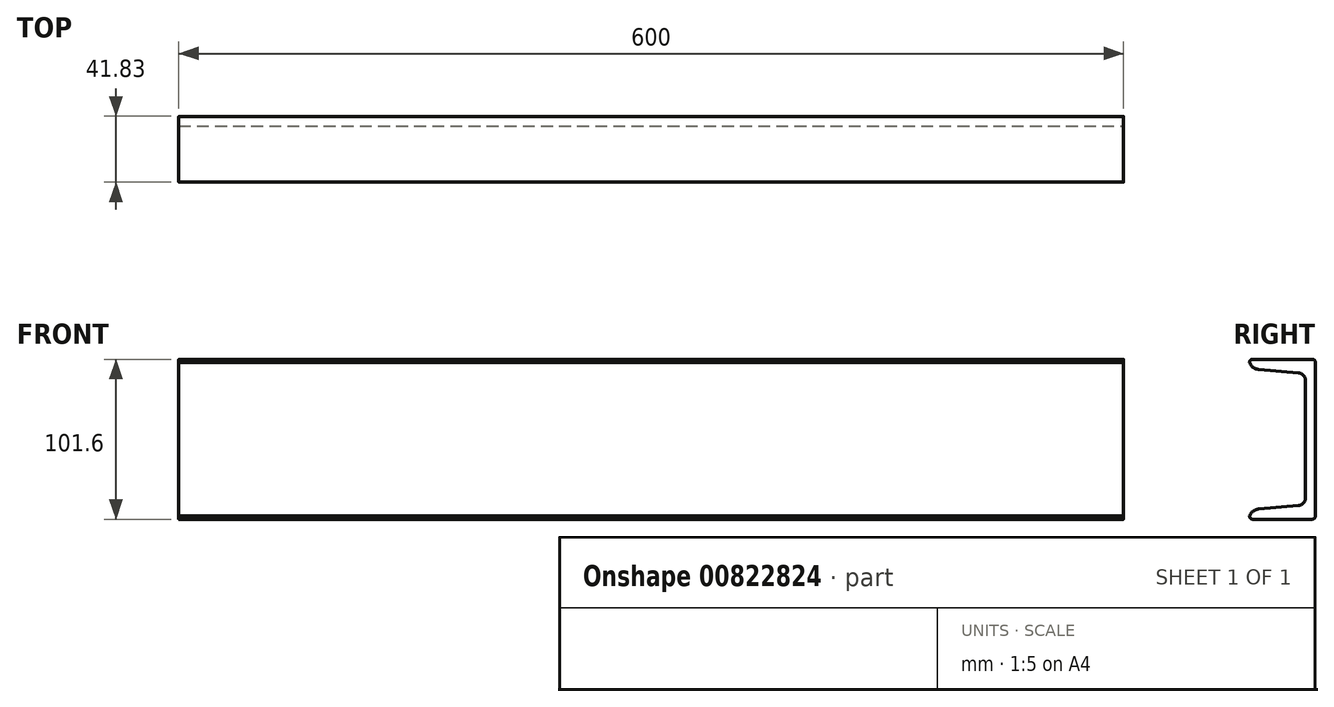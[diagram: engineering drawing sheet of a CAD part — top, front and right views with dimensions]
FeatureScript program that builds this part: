
annotation { "Feature Type Name" : "Feature", "Feature Type Description" : "" }
export const myFeature = defineFeature(function(context is Context, id is Id, definition is map)
    precondition{}
    {
        {
            var Q0;
            Q0=qCreatedBy(makeId("Right.planeOp"),FACE);
            var sketch = newSketch(context, id + "F0", { "sketchPlane" : qUnion([Q0])});
            skLineSegment(sketch, "E0.bottom", {"start": v(-18.91, -50.8) * mm, "end": v(18.92, -50.8) * mm});
            skLineSegment(sketch, "E0.top", {"start": v(-18.91, 50.8) * mm, "end": v(18.92, 50.8) * mm});
            skLineSegment(sketch, "E0.left", {"start": v(-20.91, -44.84) * mm, "end": v(-20.91, 44.84) * mm, "construction": true});
            skLineSegment(sketch, "E0.right", {"start": v(20.92, -48.8) * mm, "end": v(20.92, 48.8) * mm});
            skPoint(sketch, "E0.middle", {"position": v(0, 0) * mm});
            skLineSegment(sketch, "E1", {"start": v(-20.91, -44.84) * mm, "end": v(10.08, -42.12) * mm});
            skLineSegment(sketch, "E2", {"start": v(14.64, -37.14) * mm, "end": v(14.64, 37.14) * mm});
            skLineSegment(sketch, "E3", {"start": v(10.08, 42.12) * mm, "end": v(-20.92, 44.84) * mm});
            skLineSegment(sketch, "E4", {"start": v(-20.91, 44.84) * mm, "end": v(-20.91, 48.8) * mm});
            skLineSegment(sketch, "E5", {"start": v(-20.91, -44.84) * mm, "end": v(-20.91, -48.8) * mm});
            skPoint(sketch, "E6", {"position": v(-3.13, -43.28) * mm});
            skPoint(sketch, "E7", {"position": v(-3.14, 43.28) * mm});
            skPoint(sketch, "E8.visualSharp", {"position": v(20.92, 50.8) * mm});
            skArc(sketch, "E8.filletArc", {"start": v(20.92, 48.8) * mm, "mid": v(20.33, 50.21) * mm, "end": v(18.92, 50.8) * mm});
            skPoint(sketch, "E9.visualSharp", {"position": v(20.92, -50.8) * mm});
            skArc(sketch, "E9.filletArc", {"start": v(18.92, -50.8) * mm, "mid": v(20.33, -50.21) * mm, "end": v(20.92, -48.8) * mm});
            skPoint(sketch, "E10.visualSharp", {"position": v(-20.91, 50.8) * mm});
            skArc(sketch, "E10.filletArc", {"start": v(-18.91, 50.8) * mm, "mid": v(-20.33, 50.21) * mm, "end": v(-20.92, 48.8) * mm});
            skPoint(sketch, "E11.visualSharp", {"position": v(-20.91, -50.8) * mm});
            skArc(sketch, "E11.filletArc", {"start": v(-20.92, -48.8) * mm, "mid": v(-20.33, -50.21) * mm, "end": v(-18.91, -50.8) * mm});
            skPoint(sketch, "E12.visualSharp", {"position": v(14.65, -41.72) * mm});
            skArc(sketch, "E12.filletArc", {"start": v(10.08, -42.12) * mm, "mid": v(13.33, -40.52) * mm, "end": v(14.64, -37.14) * mm});
            skPoint(sketch, "E13.visualSharp", {"position": v(14.65, 41.72) * mm});
            skArc(sketch, "E13.filletArc", {"start": v(14.65, 37.14) * mm, "mid": v(13.33, 40.52) * mm, "end": v(10.08, 42.12) * mm});
            skSolve(sketch);
        }
        {
            var Q0;
            Q0=qSketchRegion(id+"F0",true);
            extrude(context, id + "F1", {"entities" : qUnion([Q0]), "endBound" : BoundingType.SYMMETRIC, "oppositeDirection" : true, "depth" : 600 * mm, "offsetDistance" : 25 * mm});
        }
        {
            var Q0;
            Q0=makeQuery(id+"F1.opExtrude","SWEPT_EDGE",EDGE,{"disambiguationData":[OSD([sQuery(id+"F0.wireOp",EDGE,"E1"),sQuery(id+"F0.wireOp",EDGE,"E5")])]});
            var Q1;
            Q1=makeQuery(id+"F1.opExtrude","SWEPT_EDGE",EDGE,{"disambiguationData":[OSD([sQuery(id+"F0.wireOp",EDGE,"E3"),sQuery(id+"F0.wireOp",EDGE,"E4")])]});
            fillet(context, id + "F2", {"entities" : qUnion([Q0, Q1]), "radius" : 7 * mm, "tangentPropagation" : true, "allowEdgeOverflow" : false});
        }
    });
